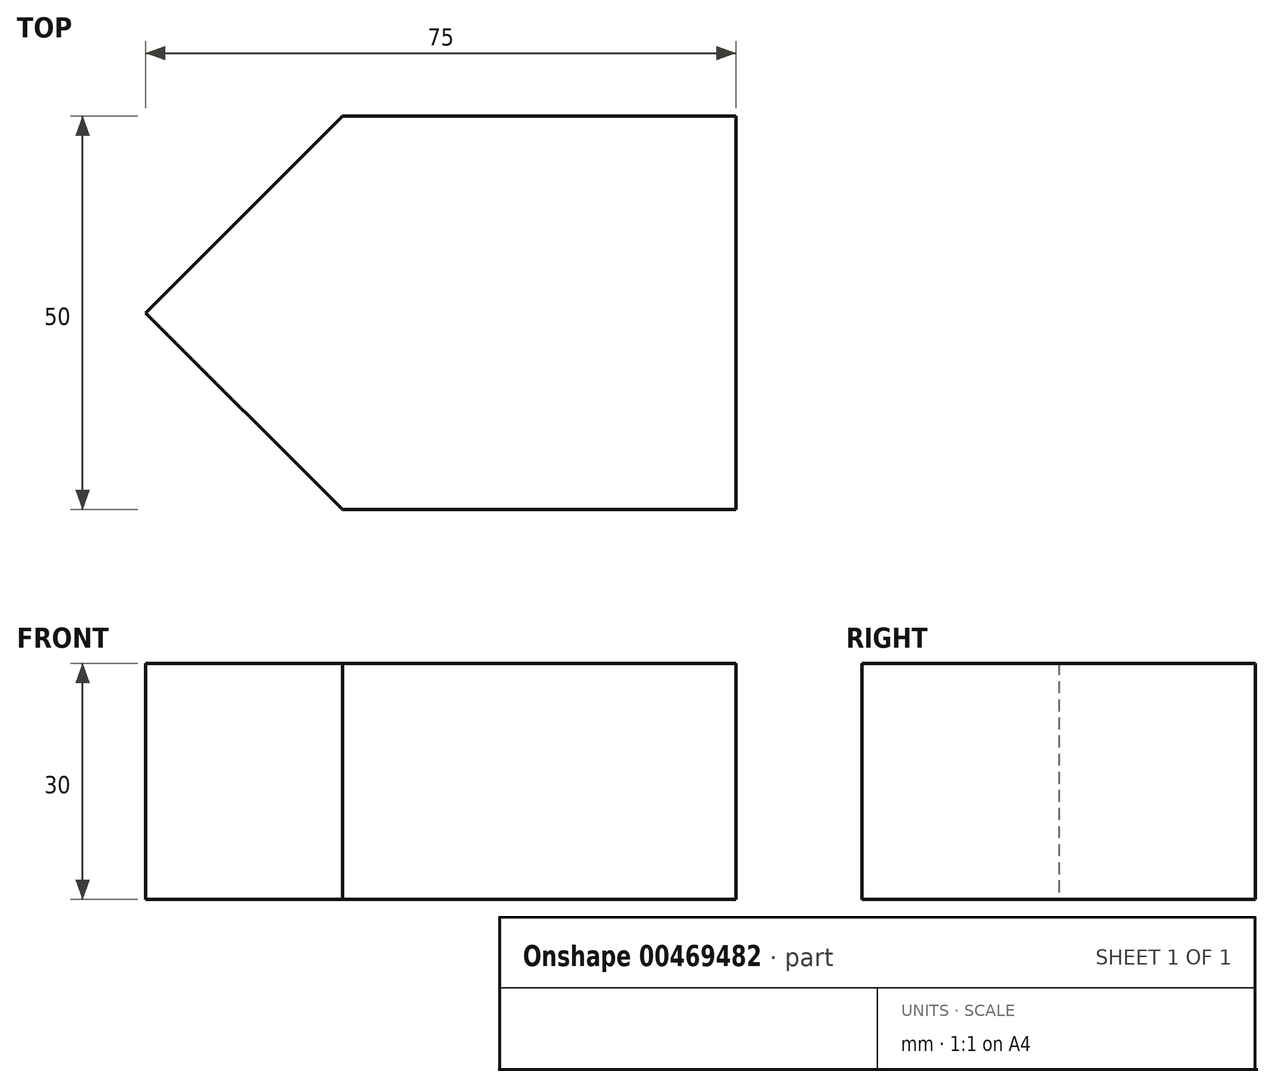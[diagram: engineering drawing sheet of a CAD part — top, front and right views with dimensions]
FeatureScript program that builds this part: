
annotation { "Feature Type Name" : "Feature", "Feature Type Description" : "" }
export const myFeature = defineFeature(function(context is Context, id is Id, definition is map)
    precondition{}
    {
        {
            var Q0;
            Q0=qCreatedBy(makeId("Top.planeOp"),FACE);
            var sketch = newSketch(context, id + "F0", { "sketchPlane" : qUnion([Q0])});
            skLineSegment(sketch, "E0", {"start": v(0, 0) * mm, "end": v(0, 50) * mm});
            skLineSegment(sketch, "E1", {"start": v(0, 50) * mm, "end": v(-50, 50) * mm});
            skLineSegment(sketch, "E2", {"start": v(-50, 50) * mm, "end": v(-75, 25) * mm});
            skLineSegment(sketch, "E3", {"start": v(-75, 25) * mm, "end": v(-50, 0) * mm});
            skLineSegment(sketch, "E4", {"start": v(-50, 0) * mm, "end": v(0, 0) * mm});
            skSolve(sketch);
        }
        {
            var Q0;
            Q0=makeQuery(id+"F0.imprint","IMPRINT",FACE,{"disambiguationData":[TD([[makeQuery(id+"F0.imprint","IMPRINT",EDGE,{"derivedFrom":sQuery(id+"F0.wireOp",EDGE,"E0")}),1.0]])]});
            extrude(context, id + "F1", {"entities" : qUnion([Q0]), "depth" : 30 * mm});
        }
    });
